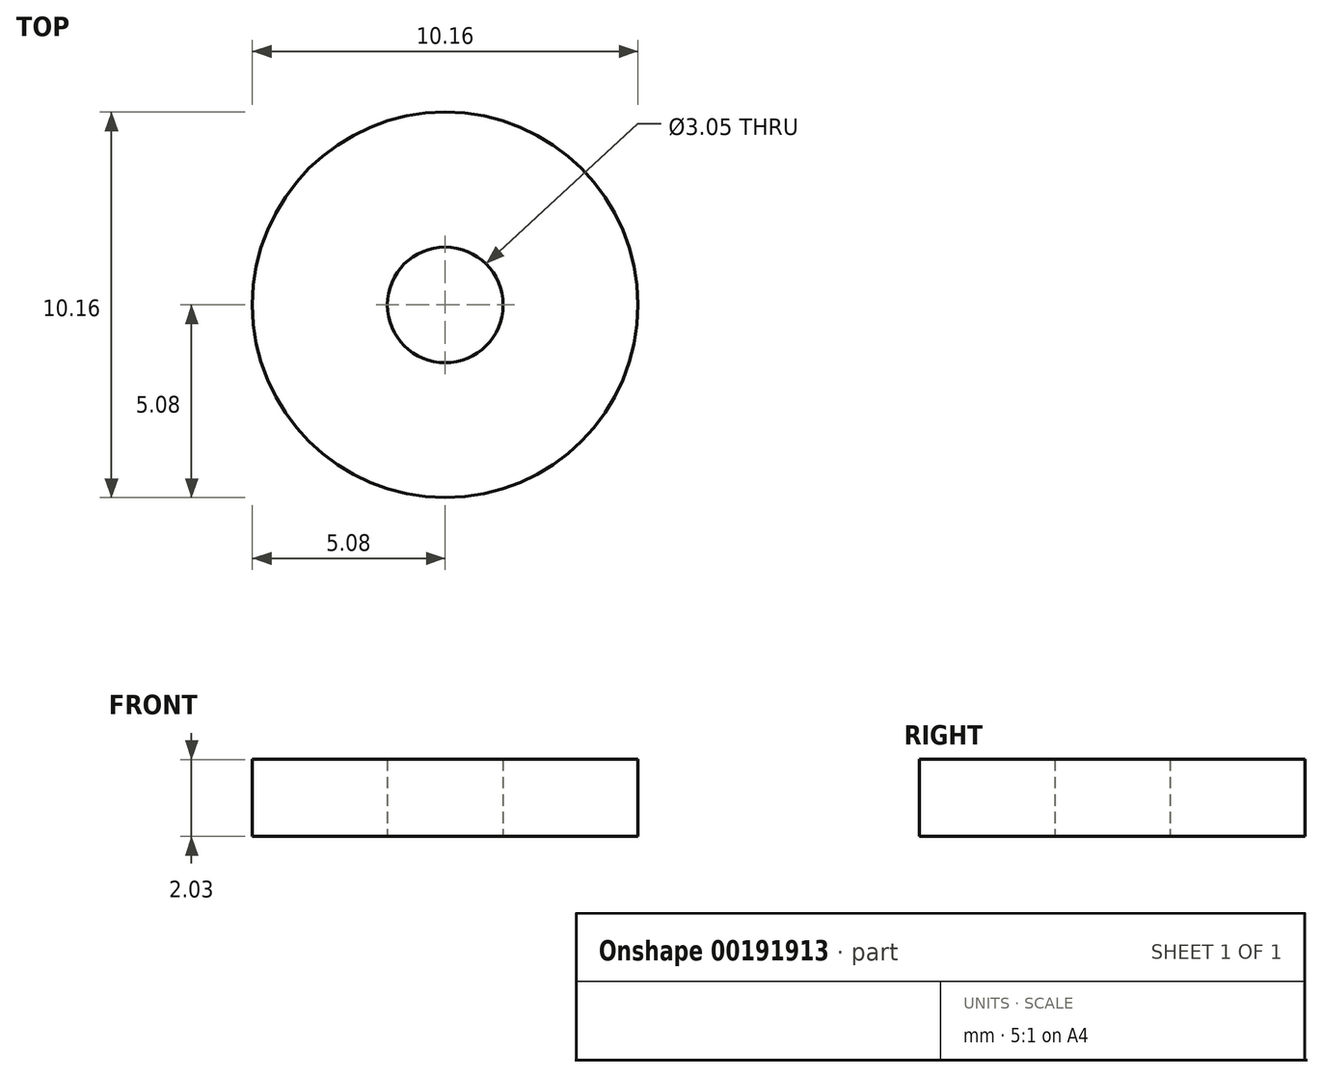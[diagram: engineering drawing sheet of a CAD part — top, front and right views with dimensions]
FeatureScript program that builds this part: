
annotation { "Feature Type Name" : "Feature", "Feature Type Description" : "" }
export const myFeature = defineFeature(function(context is Context, id is Id, definition is map)
    precondition{}
    {
        {
            var Q0;
            Q0=qCreatedBy(makeId("Top.planeOp"),FACE);
            var sketch = newSketch(context, id + "F0", { "sketchPlane" : qUnion([Q0])});
            skCircle(sketch, "E0", {"center": v(0, 0) * mm, "radius": 5.08 * mm});
            skCircle(sketch, "E1", {"center": v(0, 0) * mm, "radius": 1.52 * mm});
            skSolve(sketch);
        }
        {
            var Q0;
            Q0=makeQuery(id+"F0.imprint","IMPRINT",FACE,{"disambiguationData":[TD([[makeQuery(id+"F0.imprint","IMPRINT",EDGE,{"derivedFrom":sQuery(id+"F0.wireOp",EDGE,"E0")}),1.0]])]});
            extrude(context, id + "F1", {"entities" : qUnion([Q0]), "depth" : 2.03 * mm});
        }
    });
